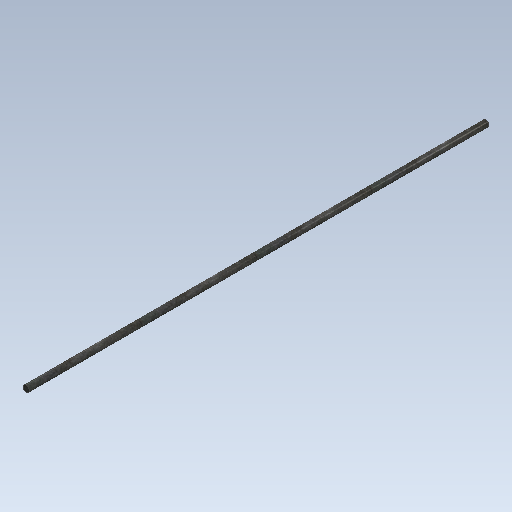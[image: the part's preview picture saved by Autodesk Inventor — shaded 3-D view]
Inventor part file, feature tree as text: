
AUTODESK INVENTOR PART (.ipt)
format: ipt  version: 2020 (Build 240168000, 168)  size: 115,712 bytes
history: native  units: mm
features: extrude x1, sketch x1
ambient origin geometry x8: Origin, YZ Plane, XZ Plane, XY Plane, X Axis, Y Axis, Z Axis, Center Point
bodies: Solid1 (feature_tree)
feature tree (2):
  extrude  "Extrusion1"  Depth=700.0mm TaperAngle=0.0deg
  sketch  "Sketch1"  dims[d0=10.0mm d1=700.0mm d2=0.0mm]
